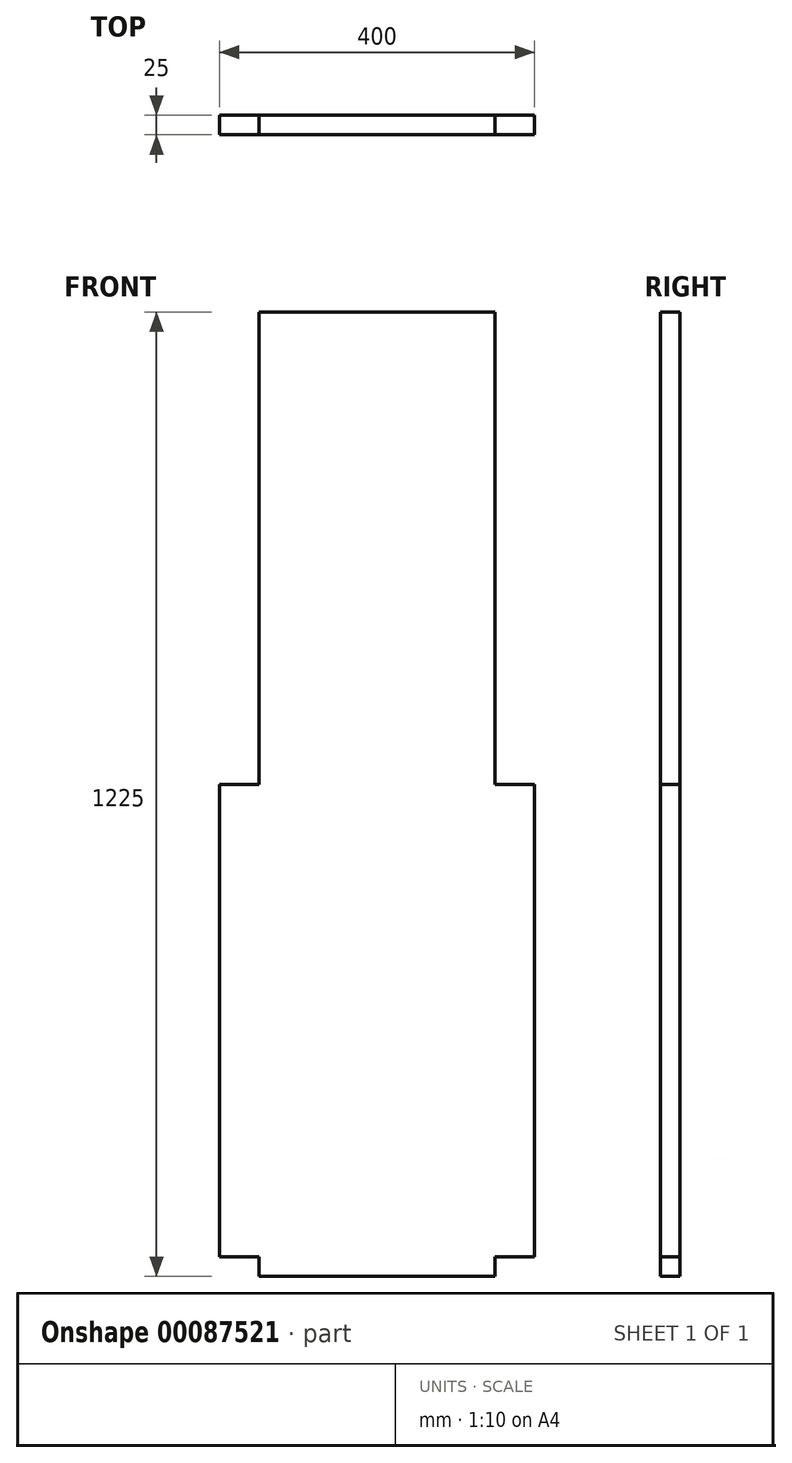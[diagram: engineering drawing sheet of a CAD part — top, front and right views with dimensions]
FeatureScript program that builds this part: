
annotation { "Feature Type Name" : "Feature", "Feature Type Description" : "" }
export const myFeature = defineFeature(function(context is Context, id is Id, definition is map)
    precondition{}
    {
        {
            var Q0;
            Q0=qCreatedBy(makeId("Front.planeOp"),FACE);
            var sketch = newSketch(context, id + "F0", { "sketchPlane" : qUnion([Q0])});
            skLineSegment(sketch, "E0.bottom", {"start": v(0, 0) * mm, "end": v(-50, 0) * mm});
            skLineSegment(sketch, "E0.top", {"start": v(0, 600) * mm, "end": v(-50, 600) * mm});
            skLineSegment(sketch, "E0.left", {"start": v(0, 0) * mm, "end": v(0, 600) * mm});
            skLineSegment(sketch, "E0.right", {"start": v(-400, 0) * mm, "end": v(-400, 600) * mm});
            skLineSegment(sketch, "E1.top", {"start": v(-350, 1200) * mm, "end": v(-50, 1200) * mm});
            skLineSegment(sketch, "E1.left", {"start": v(-350, 600) * mm, "end": v(-350, 1200) * mm});
            skLineSegment(sketch, "E1.right", {"start": v(-50, 600) * mm, "end": v(-50, 1200) * mm});
            skLineSegment(sketch, "E2.top", {"start": v(-350, -25) * mm, "end": v(-50, -25) * mm});
            skLineSegment(sketch, "E2.left", {"start": v(-350, 0) * mm, "end": v(-350, -25) * mm});
            skLineSegment(sketch, "E2.right", {"start": v(-50, 0) * mm, "end": v(-50, -25) * mm});
            skLineSegment(sketch, "E3.trimOffspring", {"start": v(-350, 0) * mm, "end": v(-400, 0) * mm});
            skLineSegment(sketch, "E4.trimOffspring", {"start": v(-350, 600) * mm, "end": v(-400, 600) * mm});
            skSolve(sketch);
        }
        {
            var Q0;
            Q0=makeQuery(id+"F0.imprint","IMPRINT",FACE,{"disambiguationData":[TD([[makeQuery(id+"F0.imprint","IMPRINT",EDGE,{"derivedFrom":sQuery(id+"F0.wireOp",EDGE,"E0.bottom")}),-1.0]])]});
            extrude(context, id + "F1", {"entities" : qUnion([Q0]), "depth" : 25 * mm});
        }
    });
